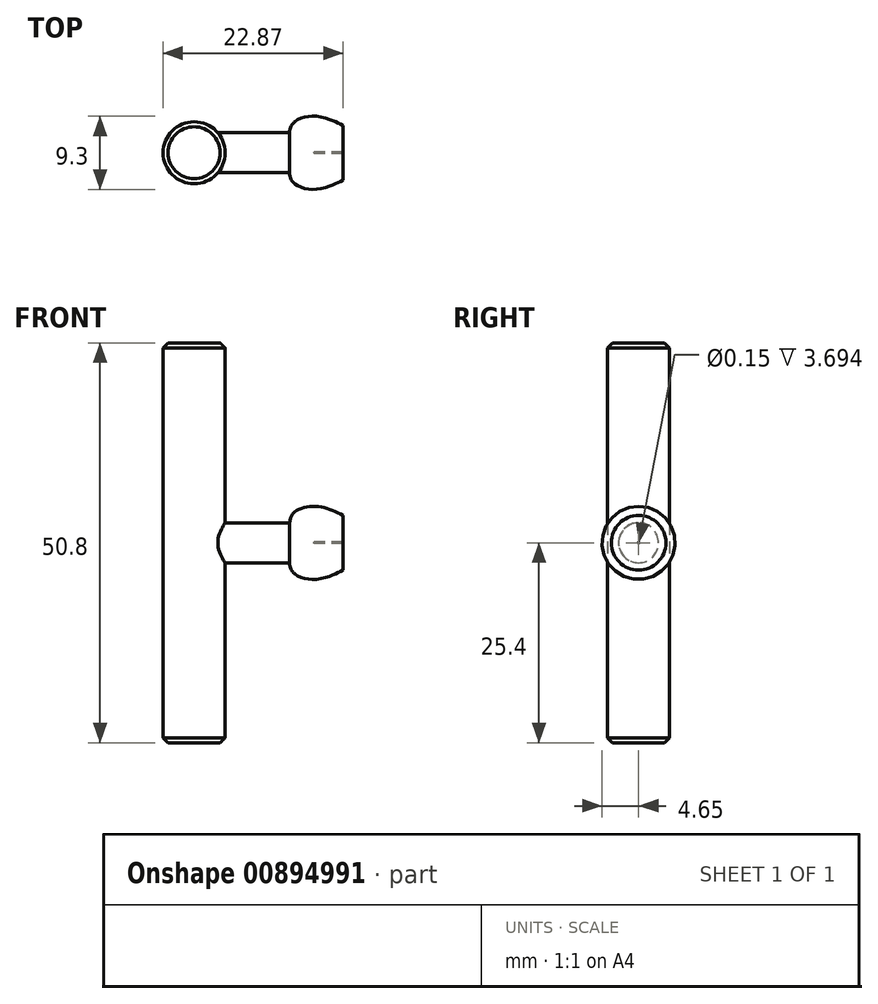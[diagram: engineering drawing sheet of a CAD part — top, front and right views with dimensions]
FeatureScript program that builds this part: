
annotation { "Feature Type Name" : "Feature", "Feature Type Description" : "" }
export const myFeature = defineFeature(function(context is Context, id is Id, definition is map)
    precondition{}
    {
        {
            var Q0;
            Q0=qCreatedBy(makeId("Top.planeOp"),FACE);
            var sketch = newSketch(context, id + "F0", { "sketchPlane" : qUnion([Q0])});
            skCircle(sketch, "E0", {"center": v(0, 0) * mm, "radius": 3.94 * mm});
            skSolve(sketch);
        }
        {
            var Q0;
            Q0=makeQuery(id+"F0.imprint","IMPRINT",FACE,{"disambiguationData":[TD([[makeQuery(id+"F0.imprint","IMPRINT",EDGE,{"derivedFrom":sQuery(id+"F0.wireOp",EDGE,"E0")}),1.0]])]});
            extrude(context, id + "F1", {"entities" : qUnion([Q0]), "depth" : 50.8 * mm, "offsetDistance" : 25.4 * mm});
        }
        {
            var Q0;
            Q0=qCreatedBy(makeId("Right.planeOp"),FACE);
            var sketch = newSketch(context, id + "F2", { "sketchPlane" : qUnion([Q0])});
            skCircle(sketch, "E1", {"center": v(0, 25.4) * mm, "radius": 2.54 * mm});
            skSolve(sketch);
        }
        {
            var Q0;
            Q0 = qSketchRegion(id + "F2", true);
            extrude(context, id + "F3", {"entities" : qUnion([Q0]), "operationType" : NewBodyOperationType.ADD, "depth" : 15.24 * mm, "offsetDistance" : 25.4 * mm});
        }
        {
            var Q0;
            Q0=qCreatedBy(makeId("Front.planeOp"),FACE);
            var sketch = newSketch(context, id + "F4", { "sketchPlane" : qUnion([Q0])});
            skLineSegment(sketch, "E2", {"start": v(12.6, 25.48) * mm, "end": v(18.93, 25.48) * mm});
            skLineSegment(sketch, "E3", {"start": v(18.93, 25.48) * mm, "end": v(18.93, 28.87) * mm});
            skFitSpline(sketch, "E4", {"points": [v(18.93, 28.87) * mm, v(15.3, 30.05) * mm, v(12.37, 28.87) * mm, v(12.6, 25.48) * mm], "startDerivative": vector(-10.02, 4.85) * mm, "endDerivative": vector(3.31, -11.6) * mm});
            skSolve(sketch);
        }
        {
            var Q0;
            Q0=makeQuery(id+"F4.imprint","IMPRINT",FACE,{"disambiguationData":[TD([[makeQuery(id+"F4.imprint","IMPRINT",EDGE,{"derivedFrom":sQuery(id+"F4.wireOp",EDGE,"E2")}),1.0]])]});
            var Q1;
            Q1=makeQuery(id+"F3.opExtrude","CAP_EDGE",EDGE,{"disambiguationData":[OSD([sQuery(id+"F2.wireOp",EDGE,"E1")])],"isStart":false});
            revolve(context, id + "F5", {"operationType" : NewBodyOperationType.ADD, "surfaceOperationType" : NewSurfaceOperationType.NEW, "entities" : qUnion([Q0]), "axis" : qUnion([Q1]), "revolveType" : RevolveType.FULL});
        }
        {
            var Q0;
            Q0=makeQuery(id+"F1.opExtrude","CAP_EDGE",EDGE,{"disambiguationData":[OSD([sQuery(id+"F0.wireOp",EDGE,"E0")])],"isStart":false});
            var Q1;
            Q1=makeQuery(id+"F1.opExtrude","CAP_EDGE",EDGE,{"disambiguationData":[OSD([sQuery(id+"F0.wireOp",EDGE,"E0")])],"isStart":true});
            chamfer(context, id + "F6", {"entities" : qUnion([Q0, Q1]), "width" : 0.64 * mm, "tangentPropagation" : true});
        }
    });
